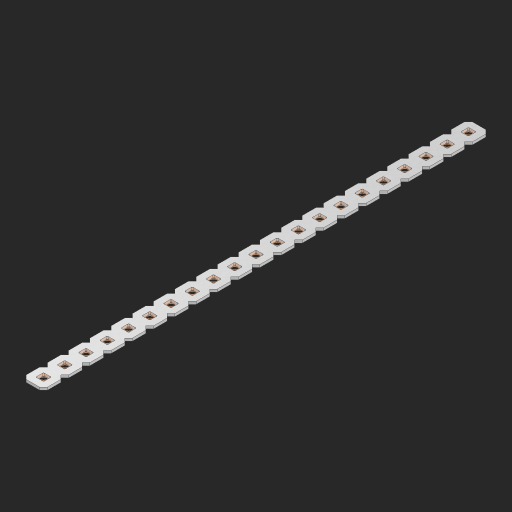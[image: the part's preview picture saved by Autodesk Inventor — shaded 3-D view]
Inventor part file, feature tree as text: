
AUTODESK INVENTOR PART (.ipt)
format: ipt  version: 2023 (Build 270158000, 158)  size: 500,224 bytes
history: native  units: in
note: dims shown in document units (in); Inventor stores cm internally (conversion verified against a paired STEP export)
features: other x22, extrude x20, sketch x2, pattern_linear x1
ambient origin geometry x8: Origin, YZ Plane, XZ Plane, XY Plane, X Axis, Y Axis, Z Axis, Center Point
bodies: Solid1 (feature_tree), Body (feature_tree)
feature tree (45):
  pattern_linear  "Rectangular Pattern1"  Spacing1=0.09in  [1 undecoded]
  sketch  "Sketch1"  dims[d1=0.5in]
  sketch  "Sketch2"  dims[d2=0.182in d3=0.09in d4=0.09in d5=0.09in d6=0.09in d7=0.09in d8=0.09in d9=0.09in d10=0.09in d11=0.02in d13=0.0in d14=0.172in d15=0.0625in d16=0.0in d19=0.5in d22=0.5in]
  other  "Srf1"
  other  "Srf126"
  other  "Srf127"
  other  "Srf128"
  other  "Srf129"
  other  "Srf130"
  other  "Srf131"
  other  "Srf250"
  other  "Srf251"
  other  "Srf252"
  other  "Srf253"
  other  "Srf254"
  other  "Srf255"
  other  "Srf256"
  other  "Srf257"
  other  "Srf258"
  other  "Srf259"
  other  "Srf260"
  other  "Srf261"
  other  "Srf262"
  other  "Srf263"
  other  "Circle"
  extrude  "ExtrusionSrf126"  Depth=0.09in
  extrude  "ExtrusionSrf127"  Depth=0.09in
  extrude  "ExtrusionSrf128"  Depth=0.09in
  extrude  "ExtrusionSrf129"  Depth=0.09in
  extrude  "ExtrusionSrf130"  Depth=0.09in
  extrude  "ExtrusionSrf131"  Depth=0.09in
  extrude  "ExtrusionSrf250"  Depth=0.09in
  extrude  "ExtrusionSrf251"  Depth=0.02in
  extrude  "ExtrusionSrf252"  TaperAngle=0.0deg  [1 undecoded]
  extrude  "ExtrusionSrf253"  Depth=0.5in
  extrude  "ExtrusionSrf254"  Depth=0.0625in TaperAngle=0.0deg
  extrude  "ExtrusionSrf255"  Depth=0.5in
  extrude  "ExtrusionSrf256"  Depth=0.5in
  extrude  "ExtrusionSrf257"  [1 undecoded]
  extrude  "ExtrusionSrf258"  [1 undecoded]
  extrude  "ExtrusionSrf259"  [1 undecoded]
  extrude  "ExtrusionSrf260"  [1 undecoded]
  extrude  "ExtrusionSrf261"  [1 undecoded]
  extrude  "ExtrusionSrf262"  [1 undecoded]
  extrude  "ExtrusionSrf263"  [1 undecoded]
note: 9 required parameter values undecoded (feature->parameter linkage not recoverable at this tier; creation-order binding heuristic only, values carry confidence <= 0.55)
